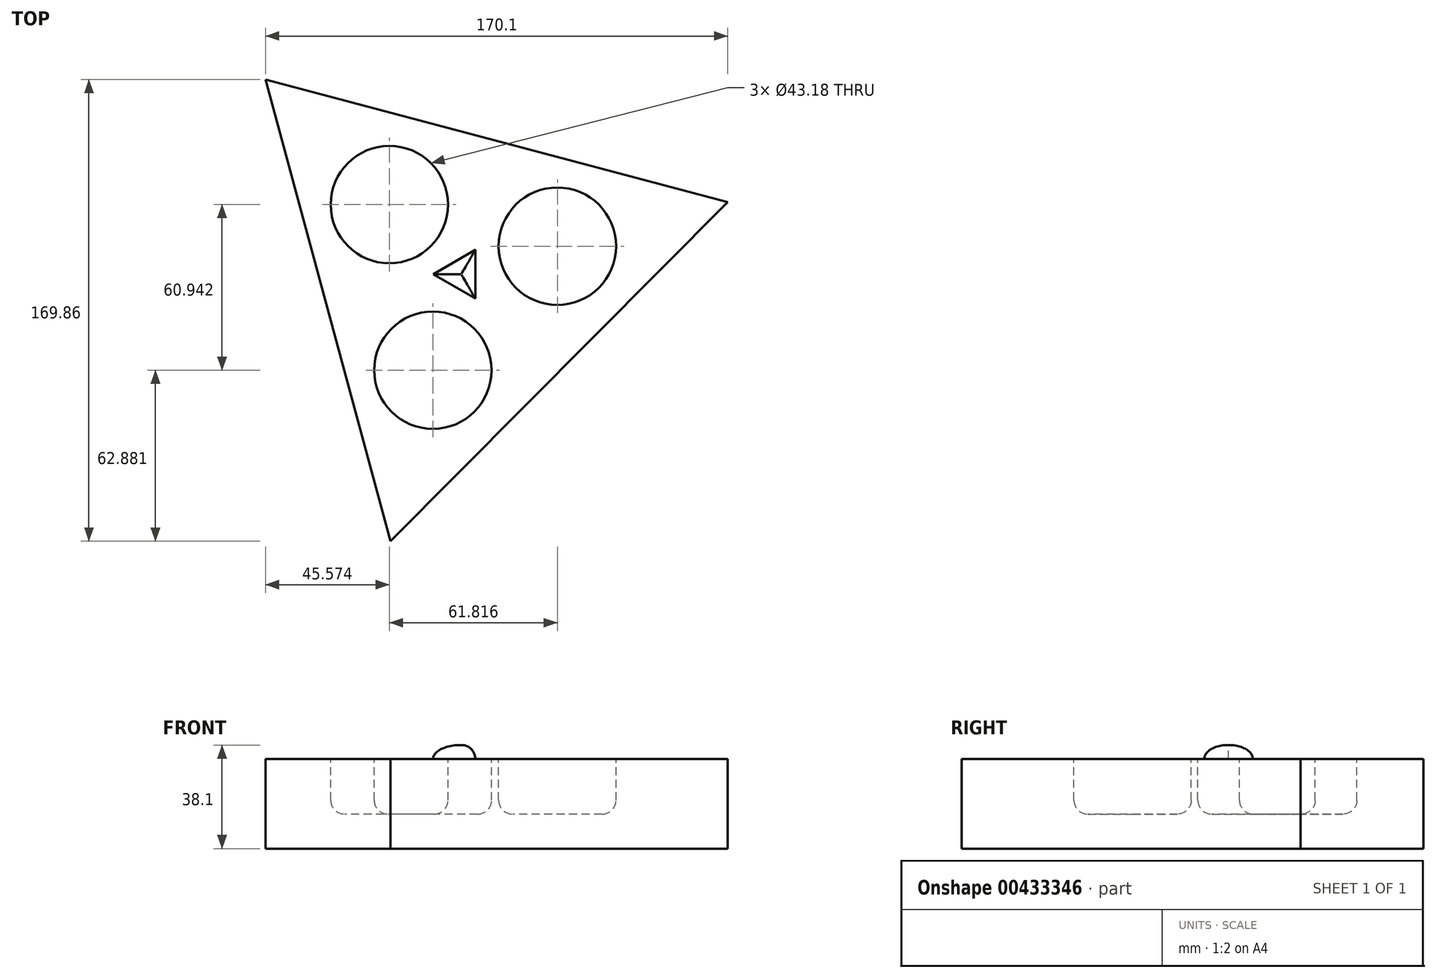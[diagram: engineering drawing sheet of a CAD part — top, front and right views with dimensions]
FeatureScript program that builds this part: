
annotation { "Feature Type Name" : "Feature", "Feature Type Description" : "" }
export const myFeature = defineFeature(function(context is Context, id is Id, definition is map)
    precondition{}
    {
        {
            var Q0;
            Q0=qCreatedBy(makeId("Top.planeOp"),FACE);
            var sketch = newSketch(context, id + "F0", { "sketchPlane" : qUnion([Q0])});
            skCircle(sketch, "E0.cCircle", {"center": v(0, 0) * mm, "radius": 50.8 * mm, "construction": true});
            skLineSegment(sketch, "E0.0", {"start": v(98.07, 26.55) * mm, "end": v(-26.04, -98.2) * mm});
            skLineSegment(sketch, "E0.1", {"start": v(-26.04, -98.2) * mm, "end": v(-72.03, 71.66) * mm});
            skLineSegment(sketch, "E0.2", {"start": v(-72.03, 71.66) * mm, "end": v(98.07, 26.55) * mm});
            skPoint(sketch, "E0.0.midPoint", {"position": v(36.01, -35.83) * mm});
            skSolve(sketch);
        }
        {
            var Q0;
            Q0=makeQuery(id+"F0.imprint","IMPRINT",FACE,{"disambiguationData":[TD([[makeQuery(id+"F0.imprint","IMPRINT",EDGE,{"derivedFrom":sQuery(id+"F0.wireOp",EDGE,"E0.0")}),-1.0]])]});
            extrude(context, id + "F1", {"entities" : qUnion([Q0]), "depth" : 33.02 * mm});
        }
        {
            var Q0;
            Q0=makeQuery(id+"F1.opExtrude","CAP_FACE",FACE,{"disambiguationData":[OSD([sQuery(id+"F0.wireOp",EDGE,"E0.0"),sQuery(id+"F0.wireOp",EDGE,"E0.1"),sQuery(id+"F0.wireOp",EDGE,"E0.2")])],"isStart":false});
            var sketch = newSketch(context, id + "F2", { "sketchPlane" : qUnion([Q0])});
            skCircle(sketch, "E1", {"center": v(-26.46, 25.62) * mm, "radius": 21.59 * mm});
            skCircle(sketch, "E2", {"center": v(-10.44, -35.32) * mm, "radius": 21.59 * mm});
            skCircle(sketch, "E3", {"center": v(35.36, 10.3) * mm, "radius": 21.59 * mm});
            skSolve(sketch);
        }
        {
            var Q0;
            Q0=makeQuery(id+"F2.imprint","IMPRINT",FACE,{"disambiguationData":[TD([[makeQuery(id+"F2.imprint","IMPRINT",EDGE,{"derivedFrom":sQuery(id+"F2.wireOp",EDGE,"E1")}),1.0]])]});
            var Q1;
            Q1=makeQuery(id+"F2.imprint","IMPRINT",FACE,{"disambiguationData":[TD([[makeQuery(id+"F2.imprint","IMPRINT",EDGE,{"derivedFrom":sQuery(id+"F2.wireOp",EDGE,"E2")}),1.0]])]});
            var Q2;
            Q2=makeQuery(id+"F2.imprint","IMPRINT",FACE,{"disambiguationData":[TD([[makeQuery(id+"F2.imprint","IMPRINT",EDGE,{"derivedFrom":sQuery(id+"F2.wireOp",EDGE,"E3")}),1.0]])]});
            extrude(context, id + "F3", {"entities" : qUnion([Q0, Q1, Q2]), "operationType" : NewBodyOperationType.REMOVE, "oppositeDirection" : true, "depth" : 20.32 * mm});
        }
        {
            var Q0;
            Q0=makeQuery(id+"F3.boolean.opBoolean","COPY",EDGE,{"derivedFrom":makeQuery(id+"F3.opExtrude","CAP_EDGE",EDGE,{"disambiguationData":[OSD([sQuery(id+"F2.wireOp",EDGE,"E1")])],"isStart":true})});
            var Q1;
            Q1=makeQuery(id+"F3.boolean.opBoolean","COPY",EDGE,{"derivedFrom":makeQuery(id+"F3.opExtrude","CAP_EDGE",EDGE,{"disambiguationData":[OSD([sQuery(id+"F2.wireOp",EDGE,"E2")])],"isStart":true})});
            var Q2;
            Q2=makeQuery(id+"F3.boolean.opBoolean","COPY",EDGE,{"derivedFrom":makeQuery(id+"F3.opExtrude","CAP_EDGE",EDGE,{"disambiguationData":[OSD([sQuery(id+"F2.wireOp",EDGE,"E3")])],"isStart":true})});
            var Q3;
            Q3=makeQuery(id+"F3.boolean.opBoolean","COPY",EDGE,{"derivedFrom":makeQuery(id+"F3.opExtrude","CAP_EDGE",EDGE,{"disambiguationData":[OSD([sQuery(id+"F2.wireOp",EDGE,"E1")])],"isStart":false})});
            var Q4;
            Q4=makeQuery(id+"F3.boolean.opBoolean","COPY",EDGE,{"derivedFrom":makeQuery(id+"F3.opExtrude","CAP_EDGE",EDGE,{"disambiguationData":[OSD([sQuery(id+"F2.wireOp",EDGE,"E2")])],"isStart":false})});
            var Q5;
            Q5=makeQuery(id+"F3.boolean.opBoolean","COPY",EDGE,{"derivedFrom":makeQuery(id+"F3.opExtrude","CAP_EDGE",EDGE,{"disambiguationData":[OSD([sQuery(id+"F2.wireOp",EDGE,"E3")])],"isStart":false})});
            fillet(context, id + "F4", {"entities" : qUnion([Q0, Q1, Q2, Q3, Q4, Q5]), "radius" : 5.08 * mm, "tangentPropagation" : true, "allowEdgeOverflow" : false});
        }
        {
            var Q0;
            Q0=makeQuery(id+"F1.opExtrude","CAP_FACE",FACE,{"disambiguationData":[OSD([sQuery(id+"F0.wireOp",EDGE,"E0.0"),sQuery(id+"F0.wireOp",EDGE,"E0.1"),sQuery(id+"F0.wireOp",EDGE,"E0.2")])],"isStart":false});
            var sketch = newSketch(context, id + "F5", { "sketchPlane" : qUnion([Q0])});
            skCircle(sketch, "E4.cCircle", {"center": v(0, 0) * mm, "radius": 5.16 * mm, "construction": true});
            skLineSegment(sketch, "E4.0", {"start": v(5.16, 8.95) * mm, "end": v(5.16, -8.95) * mm});
            skLineSegment(sketch, "E4.1", {"start": v(5.16, -8.95) * mm, "end": v(-10.33, 0) * mm});
            skLineSegment(sketch, "E4.2", {"start": v(-10.33, 0) * mm, "end": v(5.16, 8.95) * mm});
            skPoint(sketch, "E4.0.midPoint", {"position": v(5.16, 0) * mm});
            skSolve(sketch);
        }
        {
            var Q0;
            Q0=makeQuery(id+"F5.imprint","IMPRINT",FACE,{"disambiguationData":[TD([[makeQuery(id+"F5.imprint","IMPRINT",EDGE,{"derivedFrom":sQuery(id+"F5.wireOp",EDGE,"E4.0")}),-1.0]])]});
            extrude(context, id + "F6", {"entities" : qUnion([Q0]), "depth" : 5.08 * mm});
        }
        {
            var Q0;
            Q0=makeQuery(id+"F6.opExtrude","CAP_EDGE",EDGE,{"disambiguationData":[OSD([sQuery(id+"F5.wireOp",EDGE,"E4.0")])],"isStart":false});
            var Q1;
            Q1=makeQuery(id+"F6.opExtrude","CAP_EDGE",EDGE,{"disambiguationData":[OSD([sQuery(id+"F5.wireOp",EDGE,"E4.1")])],"isStart":false});
            var Q2;
            Q2=makeQuery(id+"F6.opExtrude","CAP_EDGE",EDGE,{"disambiguationData":[OSD([sQuery(id+"F5.wireOp",EDGE,"E4.2")])],"isStart":false});
            fillet(context, id + "F7", {"entities" : qUnion([Q0, Q1, Q2]), "radius" : 5.08 * mm, "tangentPropagation" : true, "allowEdgeOverflow" : false});
        }
    });
